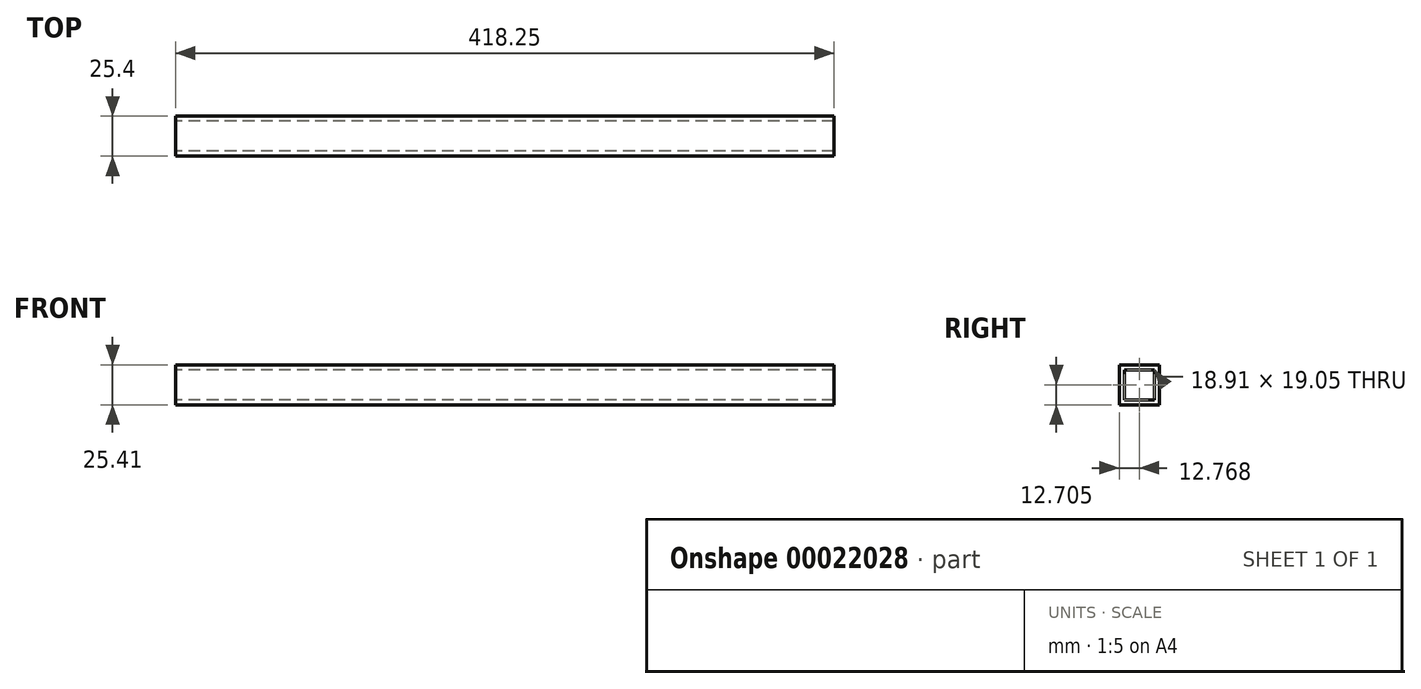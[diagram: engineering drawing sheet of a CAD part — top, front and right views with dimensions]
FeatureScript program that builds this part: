
annotation { "Feature Type Name" : "Feature", "Feature Type Description" : "" }
export const myFeature = defineFeature(function(context is Context, id is Id, definition is map)
    precondition{}
    {
        {
            var Q0;
            Q0=qCreatedBy(makeId("Right.planeOp"),FACE);
            var sketch = newSketch(context, id + "F0", { "sketchPlane" : qUnion([Q0])});
            skLineSegment(sketch, "E0.top", {"start": v(0, -3.17) * mm, "end": v(25.4, -3.17) * mm});
            skLineSegment(sketch, "E0.left", {"start": v(0, 0) * mm, "end": v(0, -3.17) * mm});
            skLineSegment(sketch, "E1.top", {"start": v(25.4, 22.23) * mm, "end": v(22.22, 22.22) * mm});
            skLineSegment(sketch, "E1.left", {"start": v(25.4, -3.17) * mm, "end": v(25.4, 22.23) * mm});
            skLineSegment(sketch, "E1.right", {"start": v(22.23, 0) * mm, "end": v(22.22, 22.22) * mm});
            skLineSegment(sketch, "E2", {"start": v(0, 0) * mm, "end": v(22.23, 0) * mm});
            skLineSegment(sketch, "E3", {"start": v(25.4, 22.22) * mm, "end": v(0, 22.22) * mm});
            skLineSegment(sketch, "E4", {"start": v(0, 22.22) * mm, "end": v(0, -3.17) * mm});
            skLineSegment(sketch, "E5", {"start": v(3.31, -3.17) * mm, "end": v(0, -3.17) * mm});
            skLineSegment(sketch, "E6", {"start": v(25.4, 22.23) * mm, "end": v(25.4, 19.05) * mm});
            skLineSegment(sketch, "E7", {"start": v(25.4, 19.05) * mm, "end": v(0, 19.05) * mm});
            skLineSegment(sketch, "E8", {"start": v(3.31, -3.17) * mm, "end": v(3.31, 22.23) * mm});
            skSolve(sketch);
        }
        {
            var Q0;
            {var subQ0=sQuery(id+"F0.wireOp",EDGE,"E4");var subQ1=sQuery(id+"F0.wireOp",EDGE,"E3");var subQ2=makeQuery(id+"F0.imprint","INTERSECT",VERTEX,{"derivedFrom":[subQ1,subQ0]});var subQ3=sQuery(id+"F0.wireOp",EDGE,"E8");var subQ5=sQuery(id+"F0.wireOp",EDGE,"E7");var subQ6=makeQuery(id+"F0.imprint","INTERSECT",VERTEX,{"derivedFrom":[subQ0,subQ5]});var subQ9=makeQuery(id+"F0.imprint","IMPRINT",EDGE,{"disambiguationData":[TD([[subQ6,1.0]])],"derivedFrom":subQ5});var subQ10=sQuery(id+"F0.wireOp",EDGE,"E1.right");var subQ11=sQuery(id+"F0.wireOp",EDGE,"E1.top");var subQ13=makeQuery(id+"F0.imprint","INTERSECT",VERTEX,{"derivedFrom":[subQ10,subQ5]});var subQ18=sQuery(id+"F0.wireOp",EDGE,"E0.top");var subQ19=makeQuery(id+"F0.imprint","INTERSECT",VERTEX,{"derivedFrom":[subQ18,subQ3]});var subQ20=sQuery(id+"F0.wireOp",EDGE,"E0.left");Q0=qUnion([makeQuery(id+"F0.imprint","IMPRINT",FACE,{"disambiguationData":[TD([[makeQuery(id+"F0.imprint","IMPRINT",EDGE,{"disambiguationData":[TD([[subQ19,-1.0]])],"derivedFrom":subQ18}),1.0]])]}),makeQuery(id+"F0.imprint","IMPRINT",FACE,{"disambiguationData":[TD([[subQ9,1.0]])]}),makeQuery(id+"F0.imprint","IMPRINT",FACE,{"disambiguationData":[TD([[makeQuery(id+"F0.imprint","IMPRINT",EDGE,{"derivedFrom":subQ20}),1.0]])]}),makeQuery(id+"F0.imprint","IMPRINT",FACE,{"disambiguationData":[TD([[makeQuery(id+"F0.imprint","IMPRINT",EDGE,{"derivedFrom":subQ11}),1.0]])]}),makeQuery(id+"F0.imprint","IMPRINT",FACE,{"disambiguationData":[TD([[makeQuery(id+"F0.imprint","IMPRINT",EDGE,{"disambiguationData":[TD([[subQ13,-1.0]])],"derivedFrom":subQ5}),-1.0]])]}),makeQuery(id+"F0.imprint","IMPRINT",FACE,{"disambiguationData":[TD([[makeQuery(id+"F0.imprint","IMPRINT",EDGE,{"disambiguationData":[TD([[subQ2,1.0]])],"derivedFrom":subQ1}),1.0]])]})]);}
            extrude(context, id + "F1", {"entities" : qUnion([Q0]), "depth" : (450 * mm - 31.75 * mm)});
        }
    });
